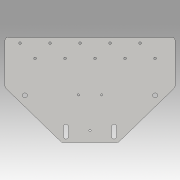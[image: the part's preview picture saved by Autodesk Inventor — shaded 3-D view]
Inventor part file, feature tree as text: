
AUTODESK INVENTOR PART (.ipt)
format: ipt  version: 2016 (Build 200138000, 138)  size: 208,384 bytes
history: native  units: in
note: dims shown in document units (in); Inventor stores cm internally (conversion verified against a paired STEP export)
features: sketch x6, extrude x3, hole x3, fillet x1
ambient origin geometry x8: Origin, YZ Plane, XZ Plane, XY Plane, X Axis, Y Axis, Z Axis, Center Point
bodies: Solid1 (feature_tree)
feature tree (13):
  extrude  "Extrusion1"  Depth=6.0in
  hole  "Hole1"  [1 undecoded]
  sketch  "Sketch3"  dims[d7=3.255in d9=2.0625in]
  sketch  "Sketch4"  dims[d10=0.2953in]
  extrude  "Extrusion3"  Depth=2.0625in
  extrude  "Extrusion5"  Depth=0.25in
  fillet  "Fillet1"  Radius=0.25in
  hole  "Hole2"  [1 undecoded]
  hole  "Hole4"  [1 undecoded]
  sketch  "Sketch1"  dims[d0=8.5in d1=6.0in]
  sketch  "Sketch2"  dims[d2=0.125in d3=0.0in d5=1.2065in]
  sketch  "Sketch5"  dims[d11=0.25in d12=0.75in d13=0.375in d14=0.25in d15=0.5635in d16=1.0in d17=0.8108in d20=0.75in d29=0.25in]
  sketch  "Sketch7"  dims[d30=0.5in d36=0.9337in d37=0.9337in d41=1.4105in d42=1.0in d43=0.0in d44=90.0deg d45=90.0deg d46=90.0deg d48=0.5in d49=0.5in d50=0.5in d53=1.0in d54=0.0in d55=0.125in d56=90.0deg d58=90.0deg d59=2.382in d60=0.118in d61=0.5805in d62=0.5805in d63=2.382in d64=0.118in d65=0.75in d66=0.375in d67=0.25in d68=0.5635in d69=1.0in d70=0.8108in d83=0.282in d84=0.75in d85=0.282in d89=1.045in d90=1.045in d94=1.5in d95=2.25in d96=3.0in d97=0.282in d98=3.75in d99=1.045in d100=4.5in d102=0.282in d103=5.25in d104=1.045in d105=6.0in d106=0.282in d107=6.75in d108=1.045in d109=7.5in d110=0.14in d111=0.75in d112=0.375in d113=0.25in d114=0.5635in d115=1.0in d116=0.8108in d117=180.0deg]
note: 3 required parameter values undecoded (feature->parameter linkage not recoverable at this tier; creation-order binding heuristic only, values carry confidence <= 0.55)
